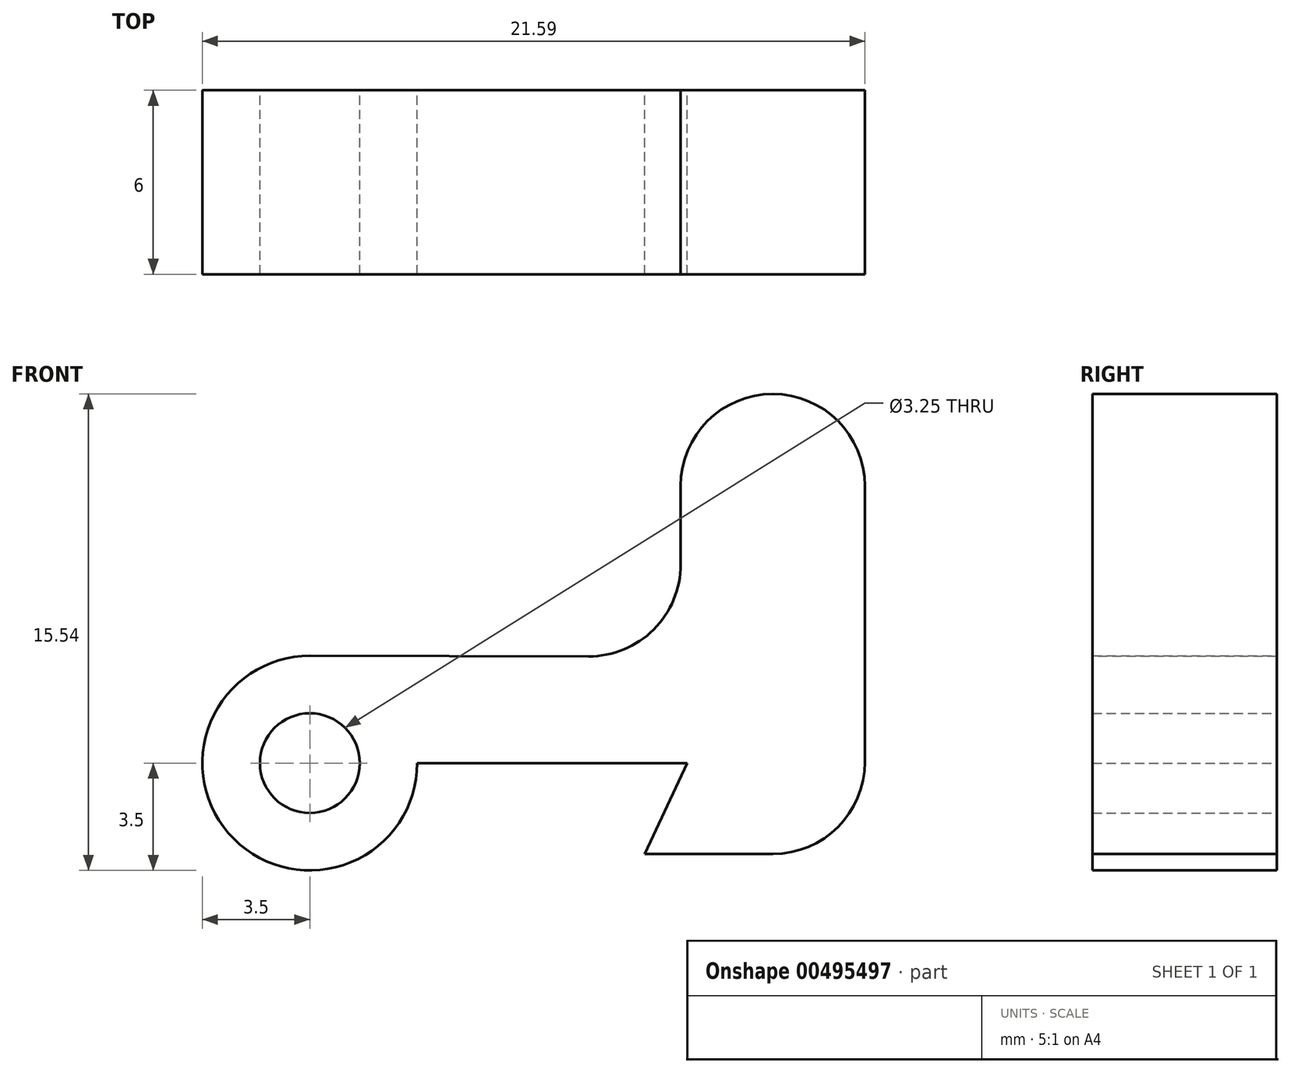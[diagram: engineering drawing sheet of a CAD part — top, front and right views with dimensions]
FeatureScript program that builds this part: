
annotation { "Feature Type Name" : "Feature", "Feature Type Description" : "" }
export const myFeature = defineFeature(function(context is Context, id is Id, definition is map)
    precondition{}
    {
        {
            var Q0;
            Q0=qCreatedBy(makeId("Front.planeOp"),FACE);
            var sketch = newSketch(context, id + "F0", { "sketchPlane" : qUnion([Q0])});
            skArc(sketch, "E0", {"start": v(0, 3.5) * mm, "mid": v(-2.48, -2.47) * mm, "end": v(3.5, 0) * mm});
            skCircle(sketch, "E1", {"center": v(0, 0) * mm, "radius": 1.63 * mm});
            skLineSegment(sketch, "E2", {"start": v(3.5, 0) * mm, "end": v(12.3, 0) * mm});
            skLineSegment(sketch, "E3", {"start": v(12.3, 0) * mm, "end": v(10.92, -2.96) * mm});
            skLineSegment(sketch, "E4", {"start": v(10.92, -2.96) * mm, "end": v(18.09, -2.96) * mm});
            skLineSegment(sketch, "E5", {"start": v(18.09, -2.96) * mm, "end": v(18.09, 12.04) * mm});
            skLineSegment(sketch, "E6", {"start": v(18.09, 12.04) * mm, "end": v(12.09, 12.04) * mm});
            skLineSegment(sketch, "E7", {"start": v(12.09, 12.04) * mm, "end": v(12.09, 3.47) * mm});
            skLineSegment(sketch, "E8", {"start": v(12.09, 3.47) * mm, "end": v(0, 3.5) * mm});
            skSolve(sketch);
        }
        {
            var Q0;
            {var subQ0=sQuery(id+"F0.wireOp",EDGE,"E0");Q0=makeQuery(id+"F0.imprint","IMPRINT",FACE,{"disambiguationData":[TD([[makeQuery(id+"F0.imprint","IMPRINT",EDGE,{"derivedFrom":subQ0}),1.0]])]});}
            extrude(context, id + "F1", {"entities" : qUnion([Q0]), "depth" : 6 * mm});
        }
        {
            var Q0;
            Q0=makeQuery(id+"F1.opExtrude","SWEPT_EDGE",EDGE,{"disambiguationData":[OSD([sQuery(id+"F0.wireOp",EDGE,"E6"),sQuery(id+"F0.wireOp",EDGE,"E7")])]});
            var Q1;
            Q1=makeQuery(id+"F1.opExtrude","SWEPT_EDGE",EDGE,{"disambiguationData":[OSD([sQuery(id+"F0.wireOp",EDGE,"E7"),sQuery(id+"F0.wireOp",EDGE,"E8")])]});
            var Q2;
            Q2=makeQuery(id+"F1.opExtrude","SWEPT_EDGE",EDGE,{"disambiguationData":[OSD([sQuery(id+"F0.wireOp",EDGE,"E5"),sQuery(id+"F0.wireOp",EDGE,"E6")])]});
            var Q3;
            Q3=makeQuery(id+"F1.opExtrude","SWEPT_EDGE",EDGE,{"disambiguationData":[OSD([sQuery(id+"F0.wireOp",EDGE,"E4"),sQuery(id+"F0.wireOp",EDGE,"E5")])]});
            fillet(context, id + "F2", {"entities" : qUnion([Q0, Q1, Q2, Q3]), "radius" : 3 * mm, "tangentPropagation" : true, "allowEdgeOverflow" : false});
        }
    });
